# Revit family: НЕВАТОМ_Клапан KD-120-AxB-F2-SN-EM-24(220)-04
name_source: partatom
category: Арматура воздуховодов
revit_build: Autodesk Revit 2017 (Build: 20170118_1100(x64)
units: mm (PartAtom-declared; Revit-internal decimal feet)

## family parameters
Всегда вертикально = Да
На основе рабочей плоскости = Нет
Общий = Нет
При загрузке вырезать с полостями = Нет
Размер круглого соединителя = Использовать диаметр
Тип детали = Вставляется

## types (1)
- НЕВАТОМ_Клапан KD-120-AxB-F2-SN-EM-24(220)-04
    ADSK_Единица измерения = шт.
    ADSK_Завод-изготовитель = НЕВАТОМ
    ADSK_Количество = 1
    ADSK_Коэффициент мощности = 1
    ADSK_Напряжение = 24 В
    ADSK_Номинальная мощность = 90 Вт
    ADSK_Полная мощность = 90 В·А
    ADSK_Предел огнестойкости = 120
    ADSK_Ток = 3 А
    U220 = Нет
    U24 = Да
    h прохода = 215 мм
    t корпуса = 218 мм
    t фланца = 3 мм
    Выбор напряжения = 1 мм
    Клапан = НЕВАТОМ_Клапан KD-120-AxB-F2-SN-EM-24(220)-04
    НЕВАТОМ_Потребляемая мощность привода = 90 Вт
